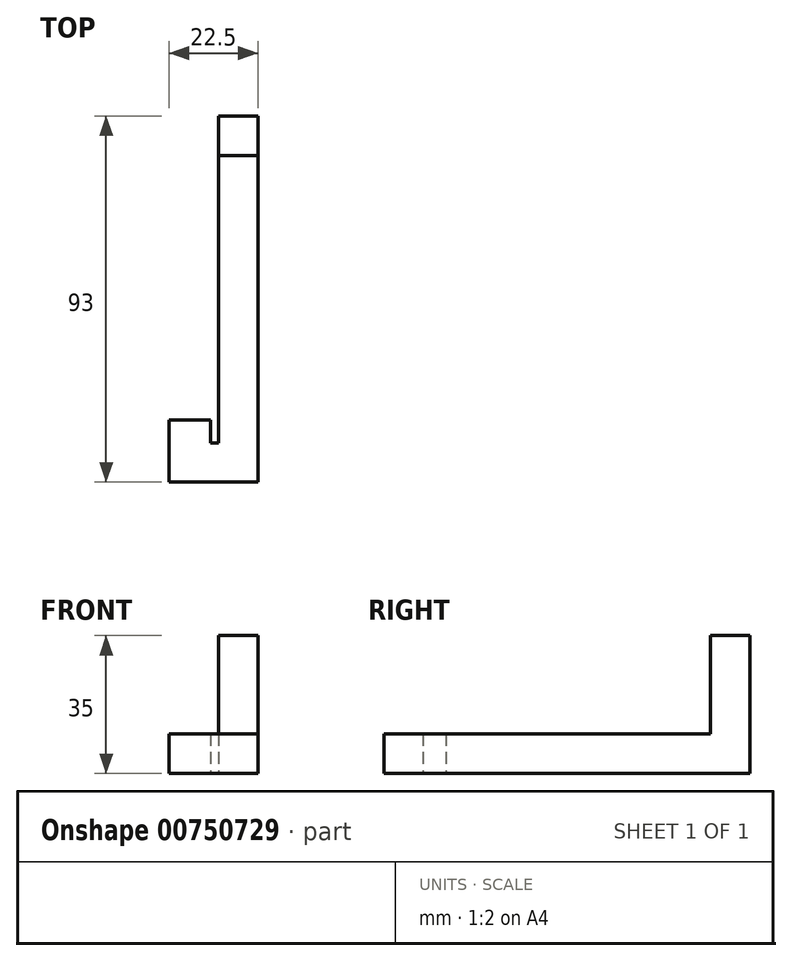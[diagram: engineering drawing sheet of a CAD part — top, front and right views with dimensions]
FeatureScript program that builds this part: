
annotation { "Feature Type Name" : "Feature", "Feature Type Description" : "" }
export const myFeature = defineFeature(function(context is Context, id is Id, definition is map)
    precondition{}
    {
        {
            var Q0;
            Q0=qCreatedBy(makeId("Top.planeOp"),FACE);
            var sketch = newSketch(context, id + "F0", { "sketchPlane" : qUnion([Q0])});
            skPoint(sketch, "E0.middle", {"position": v(0, 0) * mm});
            skLineSegment(sketch, "E1", {"start": v(22.5, 93) * mm, "end": v(22.5, 0) * mm});
            skLineSegment(sketch, "E2", {"start": v(22.5, 0) * mm, "end": v(0, 0) * mm});
            skLineSegment(sketch, "E3", {"start": v(12.5, 10) * mm, "end": v(12.5, 93) * mm});
            skLineSegment(sketch, "E4", {"start": v(12.5, 10) * mm, "end": v(10.5, 10) * mm});
            skLineSegment(sketch, "E5", {"start": v(10.5, 10) * mm, "end": v(10.5, 15.8) * mm});
            skLineSegment(sketch, "E6", {"start": v(10.5, 15.8) * mm, "end": v(0, 15.8) * mm});
            skLineSegment(sketch, "E7", {"start": v(0, 15.8) * mm, "end": v(0, 0) * mm});
            skLineSegment(sketch, "E8", {"start": v(11.5, 10) * mm, "end": v(11.5, 0) * mm, "construction": true});
            skLineSegment(sketch, "E9", {"start": v(22.5, 93) * mm, "end": v(12.5, 93) * mm});
            skSolve(sketch);
        }
        {
            var Q0;
            Q0=qSketchRegion(id+"F0",true);
            extrude(context, id + "F1", {"entities" : qUnion([Q0]), "endBound" : BoundingType.SYMMETRIC, "depth" : 10 * mm, "offsetDistance" : 25 * mm});
        }
        {
            var Q0;
            Q0=makeQuery(id+"F1.opExtrude","CAP_FACE",FACE,{"disambiguationData":[OSD([sQuery(id+"F0.wireOp",EDGE,"E1"),sQuery(id+"F0.wireOp",EDGE,"E2"),sQuery(id+"F0.wireOp",EDGE,"E3"),sQuery(id+"F0.wireOp",EDGE,"E4"),sQuery(id+"F0.wireOp",EDGE,"E5"),sQuery(id+"F0.wireOp",EDGE,"E6"),sQuery(id+"F0.wireOp",EDGE,"E7"),sQuery(id+"F0.wireOp",EDGE,"E9")])],"isStart":false});
            var sketch = newSketch(context, id + "F2", { "sketchPlane" : qUnion([Q0])});
            skLineSegment(sketch, "E10.bottom", {"start": v(12.5, 93) * mm, "end": v(22.5, 93) * mm});
            skLineSegment(sketch, "E10.top", {"start": v(12.5, 83) * mm, "end": v(22.5, 83) * mm});
            skLineSegment(sketch, "E10.left", {"start": v(12.5, 93) * mm, "end": v(12.5, 83) * mm});
            skLineSegment(sketch, "E10.right", {"start": v(22.5, 93) * mm, "end": v(22.5, 83) * mm});
            skSolve(sketch);
        }
        {
            var Q0;
            Q0 = qSketchRegion(id + "F2", true);
            extrude(context, id + "F3", {"entities" : qUnion([Q0]), "operationType" : NewBodyOperationType.ADD, "depth" : 25 * mm, "offsetDistance" : 25 * mm});
        }
    });
